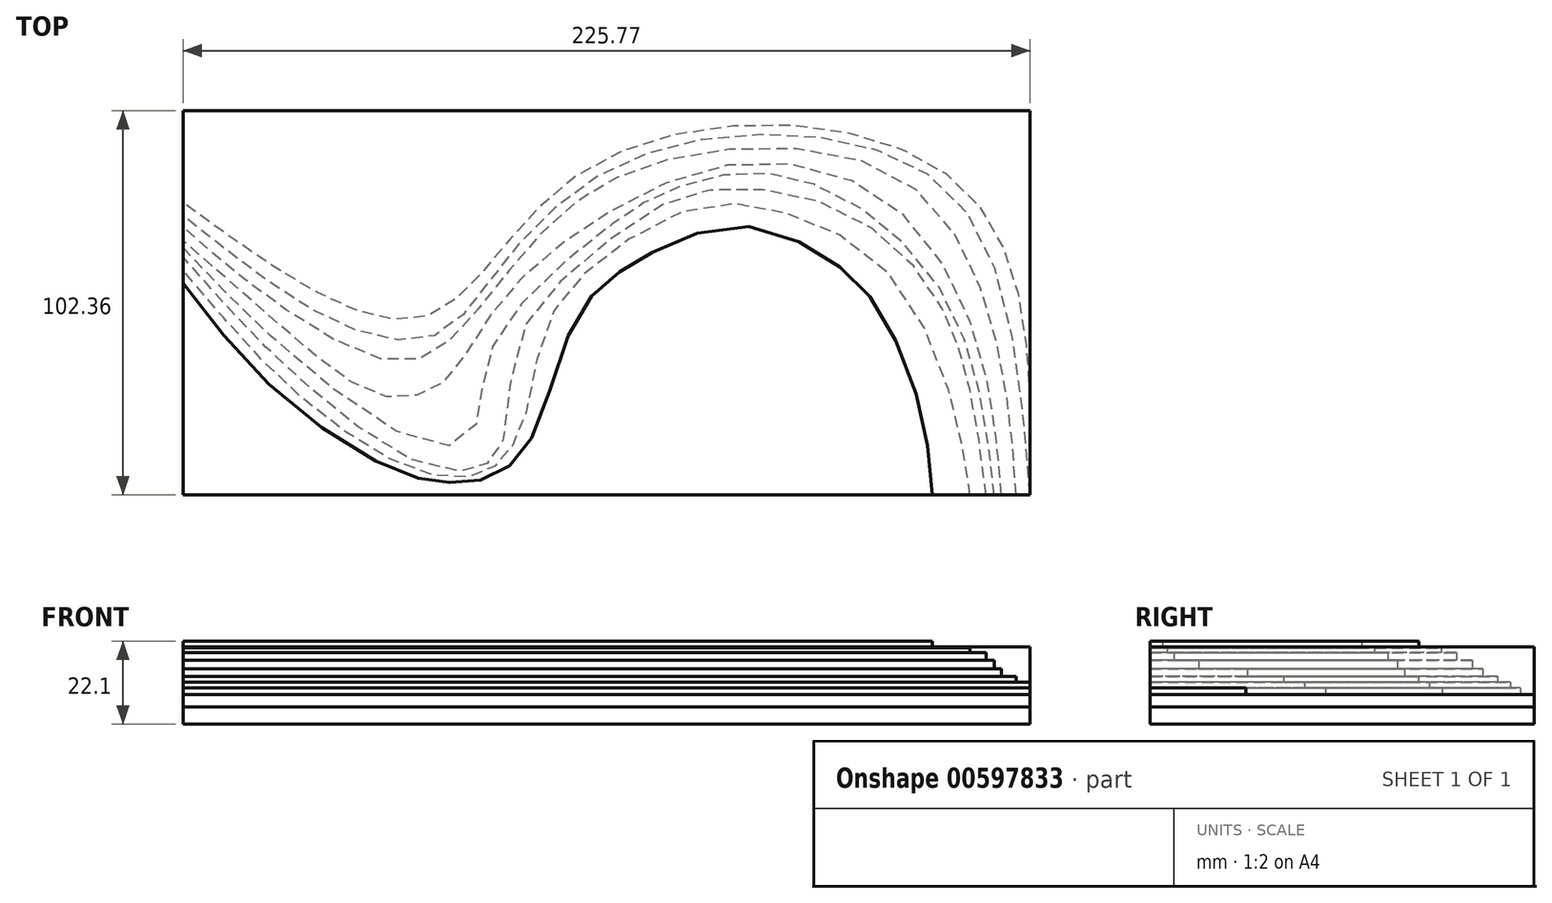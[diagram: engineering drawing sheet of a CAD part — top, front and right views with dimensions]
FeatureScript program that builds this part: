
annotation { "Feature Type Name" : "Feature", "Feature Type Description" : "" }
export const myFeature = defineFeature(function(context is Context, id is Id, definition is map)
    precondition{}
    {
        {
            var Q0;
            Q0=qCreatedBy(makeId("Top.planeOp"),FACE);
            var sketch = newSketch(context, id + "F0", { "sketchPlane" : qUnion([Q0])});
            skLineSegment(sketch, "E0.bottom", {"start": v(-122.87, 57.37) * mm, "end": v(102.9, 57.37) * mm});
            skLineSegment(sketch, "E0.top", {"start": v(-122.87, -45) * mm, "end": v(102.9, -45) * mm});
            skLineSegment(sketch, "E0.left", {"start": v(-122.87, 57.37) * mm, "end": v(-122.87, -45) * mm});
            skLineSegment(sketch, "E0.right", {"start": v(102.9, 57.37) * mm, "end": v(102.9, -45) * mm});
            skSolve(sketch);
        }
        {
            var Q0;
            Q0=makeQuery(id+"F0.imprint","IMPRINT",FACE,{"disambiguationData":[TD([[makeQuery(id+"F0.imprint","IMPRINT",EDGE,{"derivedFrom":sQuery(id+"F0.wireOp",EDGE,"E0.bottom")}),-1.0]])]});
            extrude(context, id + "F1", {"entities" : qUnion([Q0]), "depth" : 4.57 * mm, "offsetDistance" : 25.4 * mm});
        }
        {
            var Q0;
            Q0=makeQuery(id+"F1.opExtrude","CAP_FACE",FACE,{"disambiguationData":[OSD([sQuery(id+"F0.wireOp",EDGE,"E0.bottom"),sQuery(id+"F0.wireOp",EDGE,"E0.top"),sQuery(id+"F0.wireOp",EDGE,"E0.left"),sQuery(id+"F0.wireOp",EDGE,"E0.right")])],"isStart":false});
            extrude(context, id + "F2", {"entities" : qUnion([Q0]), "depth" : 3.3 * mm, "offsetDistance" : 25.4 * mm});
        }
        {
            var Q0;
            Q0=makeQuery(id+"F2.opExtrude","CAP_FACE",FACE,{"disambiguationData":[OSD([sQuery(id+"F0.wireOp",EDGE,"E0.bottom"),sQuery(id+"F0.wireOp",EDGE,"E0.top"),sQuery(id+"F0.wireOp",EDGE,"E0.left"),sQuery(id+"F0.wireOp",EDGE,"E0.right")])],"isStart":false});
            var sketch = newSketch(context, id + "F3", { "sketchPlane" : qUnion([Q0])});
            skFitSpline(sketch, "E1", {"points": [v(102.9, -45) * mm, v(82.29, 39.2) * mm, v(-15, 42) * mm, v(-58.59, 2.43) * mm, v(-122.87, 32.84) * mm], "startDerivative": vector(5.53, 379.53) * mm, "endDerivative": vector(-302.12, 220.39) * mm});
            skLineSegment(sketch, "E2", {"start": v(102.9, -45) * mm, "end": v(-122.87, -45) * mm});
            skLineSegment(sketch, "E3", {"start": v(-122.87, -45) * mm, "end": v(-122.87, 32.84) * mm});
            skSolve(sketch);
        }
        {
            var Q0;
            {var subQ4=sQuery(id+"F3.wireOp",EDGE,"E2");Q0=makeQuery(id+"F3.imprint","IMPRINT",FACE,{"disambiguationData":[TD([[makeQuery(id+"F3.imprint","IMPRINT",EDGE,{"derivedFrom":subQ4}),1.0]])]});}
            extrude(context, id + "F4", {"entities" : qUnion([Q0]), "depth" : 1.78 * mm, "offsetDistance" : 25.4 * mm});
        }
        {
            var Q0;
            Q0=makeQuery(id+"F4.opExtrude","CAP_FACE",FACE,{"disambiguationData":[OSD([sQuery(id+"F0.wireOp",EDGE,"E0.right"),sQuery(id+"F3.wireOp",EDGE,"E1"),sQuery(id+"F3.wireOp",EDGE,"E2"),sQuery(id+"F3.wireOp",EDGE,"E3")])],"isStart":false});
            var sketch = newSketch(context, id + "F5", { "sketchPlane" : qUnion([Q0])});
            skFitSpline(sketch, "E4", {"points": [v(102.9, -45) * mm, v(84.85, 31.85) * mm, v(40.9, 50.7) * mm, v(-8.62, 41.97) * mm, v(-38.97, 14.98) * mm, v(-55.43, -2.37) * mm, v(-79.66, 0) * mm, v(-107.37, 17.3) * mm, v(-122.87, 29.43) * mm], "startDerivative": vector(-40.88, 500.73) * mm, "endDerivative": vector(-157.97, 125.95) * mm});
            skLineSegment(sketch, "E5", {"start": v(102.9, -45) * mm, "end": v(-122.87, -45) * mm});
            skSolve(sketch);
        }
        {
            var Q0;
            {var subQ0=sQuery(id+"F5.wireOp",EDGE,"E4");Q0=makeQuery(id+"F5.imprint","IMPRINT",FACE,{"disambiguationData":[TD([[makeQuery(id+"F5.imprint","IMPRINT",EDGE,{"derivedFrom":subQ0}),1.0]])]});}
            extrude(context, id + "F6", {"entities" : qUnion([Q0]), "depth" : 1.52 * mm, "offsetDistance" : 25.4 * mm});
        }
        {
            var Q0;
            Q0=makeQuery(id+"F6.opExtrude","CAP_FACE",FACE,{"disambiguationData":[OSD([sQuery(id+"F3.wireOp",EDGE,"E3"),sQuery(id+"F5.wireOp",EDGE,"E4"),sQuery(id+"F5.wireOp",EDGE,"E5")])],"isStart":false});
            var sketch = newSketch(context, id + "F7", { "sketchPlane" : qUnion([Q0])});
            skFitSpline(sketch, "E6", {"points": [v(99.15, -45) * mm, v(94.42, -6.43) * mm, v(69.07, 38.82) * mm, v(7.64, 44.58) * mm, v(-25.32, 26.84) * mm, v(-48.1, 0) * mm, v(-65.77, -9.5) * mm, v(-102.35, 9.3) * mm, v(-122.87, 26.44) * mm], "startDerivative": vector(-19.18, 289.7) * mm, "endDerivative": vector(-168.88, 151.86) * mm});
            skLineSegment(sketch, "E7", {"start": v(99.15, -45) * mm, "end": v(-122.87, -45) * mm});
            skSolve(sketch);
        }
        {
            var Q0;
            {var subQ0=sQuery(id+"F7.wireOp",EDGE,"E6");Q0=makeQuery(id+"F7.imprint","IMPRINT",FACE,{"disambiguationData":[TD([[makeQuery(id+"F7.imprint","IMPRINT",EDGE,{"derivedFrom":subQ0}),1.0]])]});}
            extrude(context, id + "F8", {"entities" : qUnion([Q0]), "depth" : 1.52 * mm, "offsetDistance" : 25.4 * mm});
        }
        {
            var Q0;
            Q0=makeQuery(id+"F8.opExtrude","CAP_FACE",FACE,{"disambiguationData":[OSD([sQuery(id+"F3.wireOp",EDGE,"E3"),sQuery(id+"F7.wireOp",EDGE,"E6"),sQuery(id+"F7.wireOp",EDGE,"E7")])],"isStart":false});
            var sketch = newSketch(context, id + "F9", { "sketchPlane" : qUnion([Q0])});
            skFitSpline(sketch, "E8", {"points": [v(95.29, -45) * mm, v(89.31, -6.08) * mm, v(66.28, 32.05) * mm, v(23.83, 43.07) * mm, v(-17.24, 25.24) * mm, v(-39.74, 4.53) * mm, v(-52.12, -13.71) * mm, v(-60.5, -18.4) * mm, v(-71.47, -18.18) * mm, v(-89.93, -5.85) * mm, v(-108.3, 10.08) * mm, v(-122.87, 22.79) * mm], "startDerivative": vector(-28.76, 348.57) * mm, "endDerivative": vector(-183.94, 160.09) * mm});
            skLineSegment(sketch, "E9", {"start": v(95.29, -45) * mm, "end": v(-122.87, -45) * mm});
            skSolve(sketch);
        }
        {
            var Q0;
            Q0 = qSketchRegion(id + "F9", true);
            var Q1;
            {var subQ0=sQuery(id+"F9.wireOp",EDGE,"E8");Q1=makeQuery(id+"F9.imprint","IMPRINT",FACE,{"disambiguationData":[TD([[makeQuery(id+"F9.imprint","IMPRINT",EDGE,{"derivedFrom":subQ0}),1.0]])]});}
            extrude(context, id + "F10", {"entities" : qUnion([Q0, Q1]), "depth" : 2.03 * mm, "offsetDistance" : 25.4 * mm});
        }
        {
            var Q0;
            Q0=makeQuery(id+"F10.opExtrude","CAP_FACE",FACE,{"disambiguationData":[OSD([sQuery(id+"F3.wireOp",EDGE,"E3"),sQuery(id+"F9.wireOp",EDGE,"E8"),sQuery(id+"F9.wireOp",EDGE,"E9")])],"isStart":false});
            var sketch = newSketch(context, id + "F11", { "sketchPlane" : qUnion([Q0])});
            skFitSpline(sketch, "E10", {"points": [v(93.3, -45) * mm, v(90.07, -20.91) * mm, v(80.58, 7) * mm, v(60.7, 29.32) * mm, v(38.64, 39.73) * mm, v(19.82, 39.96) * mm, v(2.93, 34.36) * mm, v(-7.46, 27.88) * mm, v(-32.58, 6.05) * mm, v(-42.78, -12.98) * mm, v(-44.74, -26.17) * mm, v(-54.7, -32) * mm, v(-96, -5.78) * mm, v(-122.87, 20.87) * mm], "startDerivative": vector(-30.81, 302.95) * mm, "endDerivative": vector(-238.74, 255.48) * mm});
            skLineSegment(sketch, "E11", {"start": v(93.3, -45) * mm, "end": v(-122.87, -45) * mm});
            skLineSegment(sketch, "E12", {"start": v(-122.87, -45) * mm, "end": v(-122.87, 20.87) * mm});
            skSolve(sketch);
        }
        {
            var Q0;
            Q0=makeQuery(id+"F11.imprint","IMPRINT",FACE,{"disambiguationData":[TD([[makeQuery(id+"F11.imprint","IMPRINT",EDGE,{"derivedFrom":sQuery(id+"F11.wireOp",EDGE,"E10")}),1.0]])]});
            extrude(context, id + "F12", {"entities" : qUnion([Q0]), "depth" : 2.3 * mm, "offsetDistance" : 25.4 * mm});
        }
        {
            var Q0;
            Q0=makeQuery(id+"F12.opExtrude","CAP_FACE",FACE,{"disambiguationData":[OSD([sQuery(id+"F11.wireOp",EDGE,"E10"),sQuery(id+"F11.wireOp",EDGE,"E11"),sQuery(id+"F11.wireOp",EDGE,"E12")])],"isStart":false});
            var sketch = newSketch(context, id + "F13", { "sketchPlane" : qUnion([Q0])});
            skFitSpline(sketch, "E13", {"points": [v(91.1, -45) * mm, v(88, -22.55) * mm, v(84.37, -7.52) * mm, v(79.18, 5.18) * mm, v(66.74, 21.25) * mm, v(44.97, 33.7) * mm, v(21.12, 36.55) * mm, v(3.75, 31.62) * mm, v(-21.65, 12.44) * mm, v(-34.1, -6.22) * mm, v(-37.99, -31.89) * mm, v(-41.36, -36.3) * mm, v(-45.24, -38.37) * mm, v(-59.76, -36.55) * mm, v(-83.6, -21) * mm, v(-103.83, -2.6) * mm, v(-122.87, 18.4) * mm], "startDerivative": vector(-41.96, 349.1) * mm, "endDerivative": vector(-250.49, 287) * mm});
            skLineSegment(sketch, "E14", {"start": v(-122.87, 18.4) * mm, "end": v(-122.87, -45) * mm});
            skSolve(sketch);
        }
        {
            var Q0;
            Q0 = qSketchRegion(id + "F13", true);
            var Q1;
            {var subQ0=sQuery(id+"F13.wireOp",EDGE,"E13");Q1=makeQuery(id+"F13.imprint","IMPRINT",FACE,{"disambiguationData":[TD([[makeQuery(id+"F13.imprint","IMPRINT",EDGE,{"derivedFrom":subQ0}),1.0]])]});}
            extrude(context, id + "F14", {"entities" : qUnion([Q0, Q1]), "depth" : 2.03 * mm, "offsetDistance" : 25.4 * mm});
        }
        {
            var Q0;
            Q0=makeQuery(id+"F14.opExtrude","CAP_FACE",FACE,{"disambiguationData":[OSD([sQuery(id+"F11.wireOp",EDGE,"E11"),sQuery(id+"F13.wireOp",EDGE,"E13"),sQuery(id+"F13.wireOp",EDGE,"E14")])],"isStart":false});
            var sketch = newSketch(context, id + "F15", { "sketchPlane" : qUnion([Q0])});
            skFitSpline(sketch, "E15", {"points": [v(86.9, -45) * mm, v(82.13, -20.35) * mm, v(65.08, 14.11) * mm, v(38.5, 29.88) * mm, v(13.75, 31.53) * mm, v(-12.46, 16.86) * mm, v(-26.02, 0) * mm, v(-31.7, -24.01) * mm, v(-36.29, -33.73) * mm, v(-40.69, -37.94) * mm, v(-47.47, -40.33) * mm, v(-60.66, -38.5) * mm, v(-81.01, -27.13) * mm, v(-101.17, -9.71) * mm, v(-122.87, 14.85) * mm], "startDerivative": vector(-42.14, 298.14) * mm, "endDerivative": vector(-244.93, 291.15) * mm});
            skLineSegment(sketch, "E16", {"start": v(-122.87, 14.85) * mm, "end": v(-122.87, -45) * mm});
            skLineSegment(sketch, "E17", {"start": v(-122.87, -45) * mm, "end": v(86.9, -45) * mm});
            skSolve(sketch);
        }
        {
            var Q0;
            Q0=makeQuery(id+"F15.imprint","IMPRINT",FACE,{"disambiguationData":[TD([[makeQuery(id+"F15.imprint","IMPRINT",EDGE,{"derivedFrom":sQuery(id+"F15.wireOp",EDGE,"E15")}),1.0]])]});
            extrude(context, id + "F16", {"entities" : qUnion([Q0]), "depth" : 1.27 * mm, "offsetDistance" : 25.4 * mm});
        }
        {
            var Q0;
            Q0=makeQuery(id+"F16.opExtrude","CAP_FACE",FACE,{"disambiguationData":[OSD([sQuery(id+"F15.wireOp",EDGE,"E15"),sQuery(id+"F15.wireOp",EDGE,"E16"),sQuery(id+"F15.wireOp",EDGE,"E17")])],"isStart":false});
            var sketch = newSketch(context, id + "F17", { "sketchPlane" : qUnion([Q0])});
            skFitSpline(sketch, "E18", {"points": [v(76.8, -45) * mm, v(73.33, -20.9) * mm, v(61.96, 5.32) * mm, v(49.31, 17.78) * mm, v(26.77, 26.58) * mm, v(3.49, 20.35) * mm, v(-8.42, 13.01) * mm, v(-18.32, 1.65) * mm, v(-28.22, -26.03) * mm, v(-35.74, -37.2) * mm, v(-44.53, -41.24) * mm, v(-53.7, -41.6) * mm, v(-64.7, -39.04) * mm, v(-95.13, -19.98) * mm, v(-122.87, 11.36) * mm], "startDerivative": vector(-23.72, 298.38) * mm, "endDerivative": vector(-245.67, 321.38) * mm});
            skLineSegment(sketch, "E19", {"start": v(-122.87, 11.36) * mm, "end": v(-122.87, -45) * mm});
            skLineSegment(sketch, "E20", {"start": v(-122.87, -45) * mm, "end": v(76.8, -45) * mm});
            skSolve(sketch);
        }
        {
            var Q0;
            Q0=makeQuery(id+"F17.imprint","IMPRINT",FACE,{"disambiguationData":[TD([[makeQuery(id+"F17.imprint","IMPRINT",EDGE,{"derivedFrom":sQuery(id+"F17.wireOp",EDGE,"E18")}),1.0]])]});
            extrude(context, id + "F18", {"entities" : qUnion([Q0]), "depth" : 1.78 * mm, "offsetDistance" : 25.4 * mm});
        }
        {
            var Q0;
            Q0=makeQuery(id+"F2.opExtrude","CAP_FACE",FACE,{"disambiguationData":[OSD([sQuery(id+"F0.wireOp",EDGE,"E0.bottom"),sQuery(id+"F0.wireOp",EDGE,"E0.top"),sQuery(id+"F0.wireOp",EDGE,"E0.left"),sQuery(id+"F0.wireOp",EDGE,"E0.right")])],"isStart":false});
            extrude(context, id + "F19", {"entities" : qUnion([Q0]), "depth" : 12.7 * mm, "offsetDistance" : 25.4 * mm});
        }
    });
